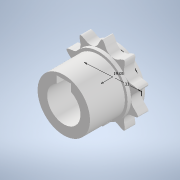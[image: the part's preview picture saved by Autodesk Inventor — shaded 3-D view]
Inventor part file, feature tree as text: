
AUTODESK INVENTOR PART (.ipt)
format: ipt  version: 2021 (Build 250183000, 183)  size: 265,728 bytes
history: native  units: in
note: dims shown in document units (in); Inventor stores cm internally (conversion verified against a paired STEP export)
features: sketch x8, extrude x4, plane x2, hole x1
ambient origin geometry x8: Origin, YZ Plane, XZ Plane, XY Plane, X Axis, Y Axis, Z Axis, Center Point
bodies: Solid1 (feature_tree)
feature tree (15):
  extrude  "Extrusion1"  Depth=1.1811in
  extrude  "Extrusion2"  Depth=0.7874in TaperAngle=0.0deg
  plane  "Work Plane1"
  sketch  "Sketch3"  dims[d6=-0.0787in d7=1.2992in]
  sketch  "Sketch4"  dims[d8=0.75in d9=0.2362in d10=0.0in]
  sketch  "Sketch5"  dims[d11=0.75in d12=0.2341in d13=0.1575in d14=0.0787in d15=90.0deg d16=0.2362in d17=0.8108in d38=0.3543in]
  sketch  "Sketch6"  dims[d39=0.3283in]
  extrude  "Extrusion3"  Depth=1.2992in
  hole  "Hole1"  [1 undecoded]
  plane  "Work Plane5"
  extrude  "Extrusion6"  Depth=0.0787in
  sketch  "Sketch1"  dims[d0=0.3937in d1=0.0in d2=1.1811in]
  sketch  "Sketch2"  dims[d3=0.75in d4=0.7874in d5=0.0in]
  sketch  "Sketch7"  dims[d40=0.1969in]
  sketch  "Sketch12"  dims[d41=0.3937in d42=0.0in d43=0.1642in d44=0.0984in d45=0.1476in d46=0.0492in d47=0.0in d48=0.0in d18=0.0295in d19=0.8108in d20=0.0025in d21=0.0295in d22=0.0148in]
note: 1 required parameter value undecoded (feature->parameter linkage not recoverable at this tier; creation-order binding heuristic only, values carry confidence <= 0.55)
